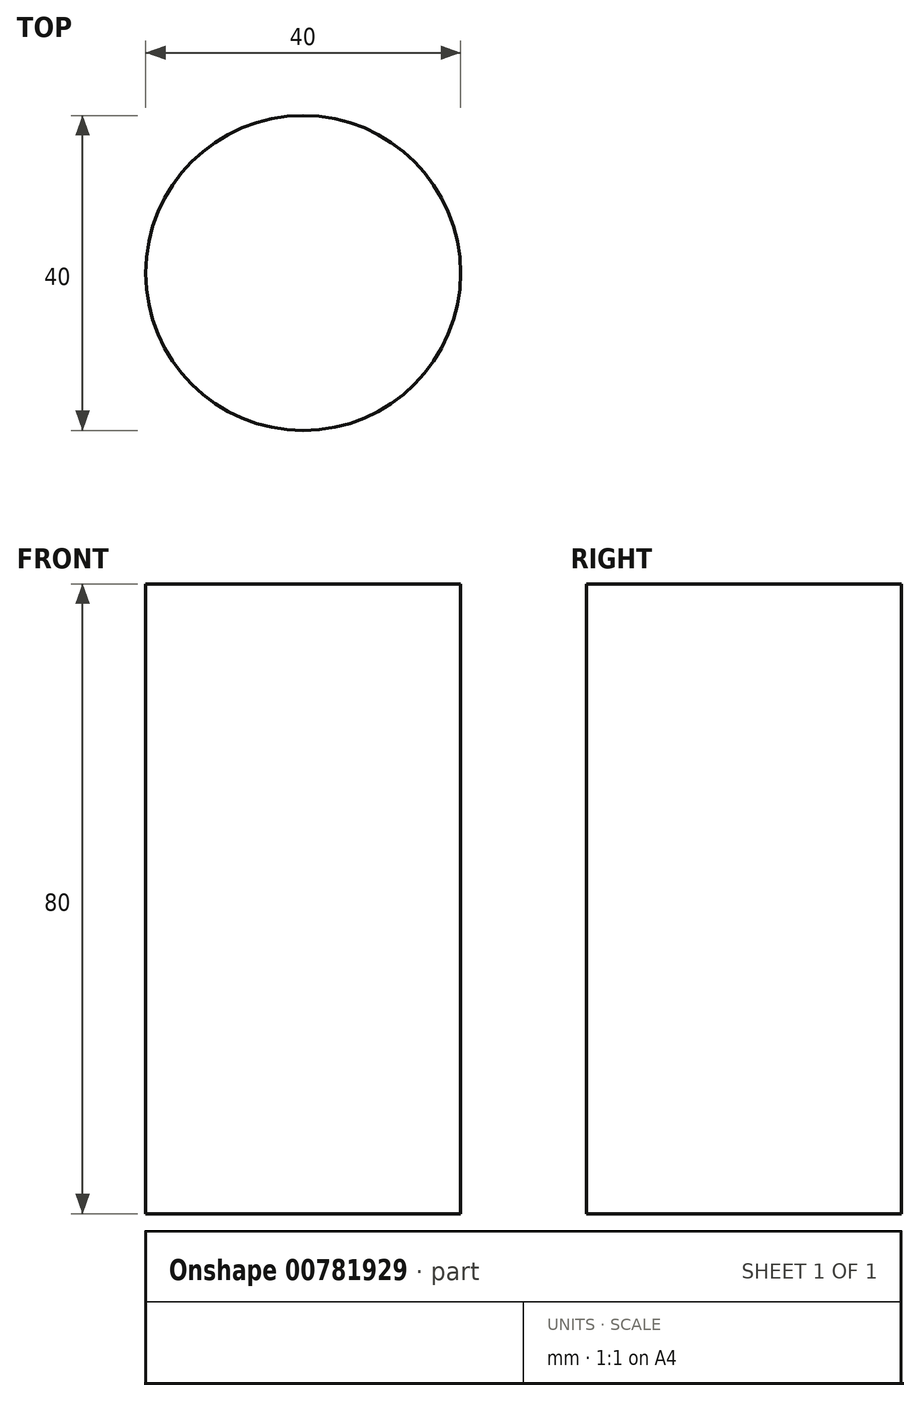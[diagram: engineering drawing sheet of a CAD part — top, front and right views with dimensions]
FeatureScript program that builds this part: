
annotation { "Feature Type Name" : "Feature", "Feature Type Description" : "" }
export const myFeature = defineFeature(function(context is Context, id is Id, definition is map)
    precondition{}
    {
        {
            var Q0;
            Q0=qCreatedBy(makeId("Front.planeOp"),FACE);
            var sketch = newSketch(context, id + "F0", { "sketchPlane" : qUnion([Q0])});
            skLineSegment(sketch, "E0.bottom", {"start": v(0, 59.95) * mm, "end": v(20, 59.95) * mm});
            skLineSegment(sketch, "E0.top", {"start": v(0, -20.05) * mm, "end": v(20, -20.05) * mm});
            skLineSegment(sketch, "E0.left", {"start": v(0, 59.95) * mm, "end": v(0, -20.05) * mm});
            skLineSegment(sketch, "E0.right", {"start": v(20, 59.95) * mm, "end": v(20, -20.05) * mm});
            skSolve(sketch);
        }
        {
            var Q0;
            Q0=makeQuery(id+"F0.imprint","IMPRINT",FACE,{"disambiguationData":[TD([[makeQuery(id+"F0.imprint","IMPRINT",EDGE,{"derivedFrom":sQuery(id+"F0.wireOp",EDGE,"E0.bottom")}),-1.0]])]});
            var Q1;
            Q1=sQuery(id+"F0.wireOp",EDGE,"E0.left");
            revolve(context, id + "F1", {"surfaceOperationType" : NewSurfaceOperationType.NEW, "entities" : qUnion([Q0]), "axis" : qUnion([Q1]), "revolveType" : RevolveType.FULL});
        }
    });
